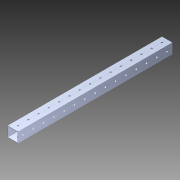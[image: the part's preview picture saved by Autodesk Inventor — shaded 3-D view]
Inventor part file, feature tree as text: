
AUTODESK INVENTOR PART (.ipt)
format: ipt  version: 2014 (Build 180170000, 170)  size: 1,200,128 bytes
history: native  units: in
note: dims shown in document units (in); Inventor stores cm internally (conversion verified against a paired STEP export)
features: pattern_circular x1, other x1, plane x1, extrude x1, imported_body x1, sketch x1
ambient origin geometry x8: Origin, YZ Plane, XZ Plane, XY Plane, X Axis, Y Axis, Z Axis, Center Point
bodies: Body1 (feature_tree)
feature tree (6):
  pattern_circular  "CirPattern2"
  other  "217-3426-STEP1"
  plane  "Work Plane1"
  extrude  "Extrusion1"  Depth=3937.0079in TaperAngle=0.0deg
  imported_body  "Base1"
  sketch  "Sketch1"  dims[d0=-15.0in d1=3937.0079in d2=0.0in]
